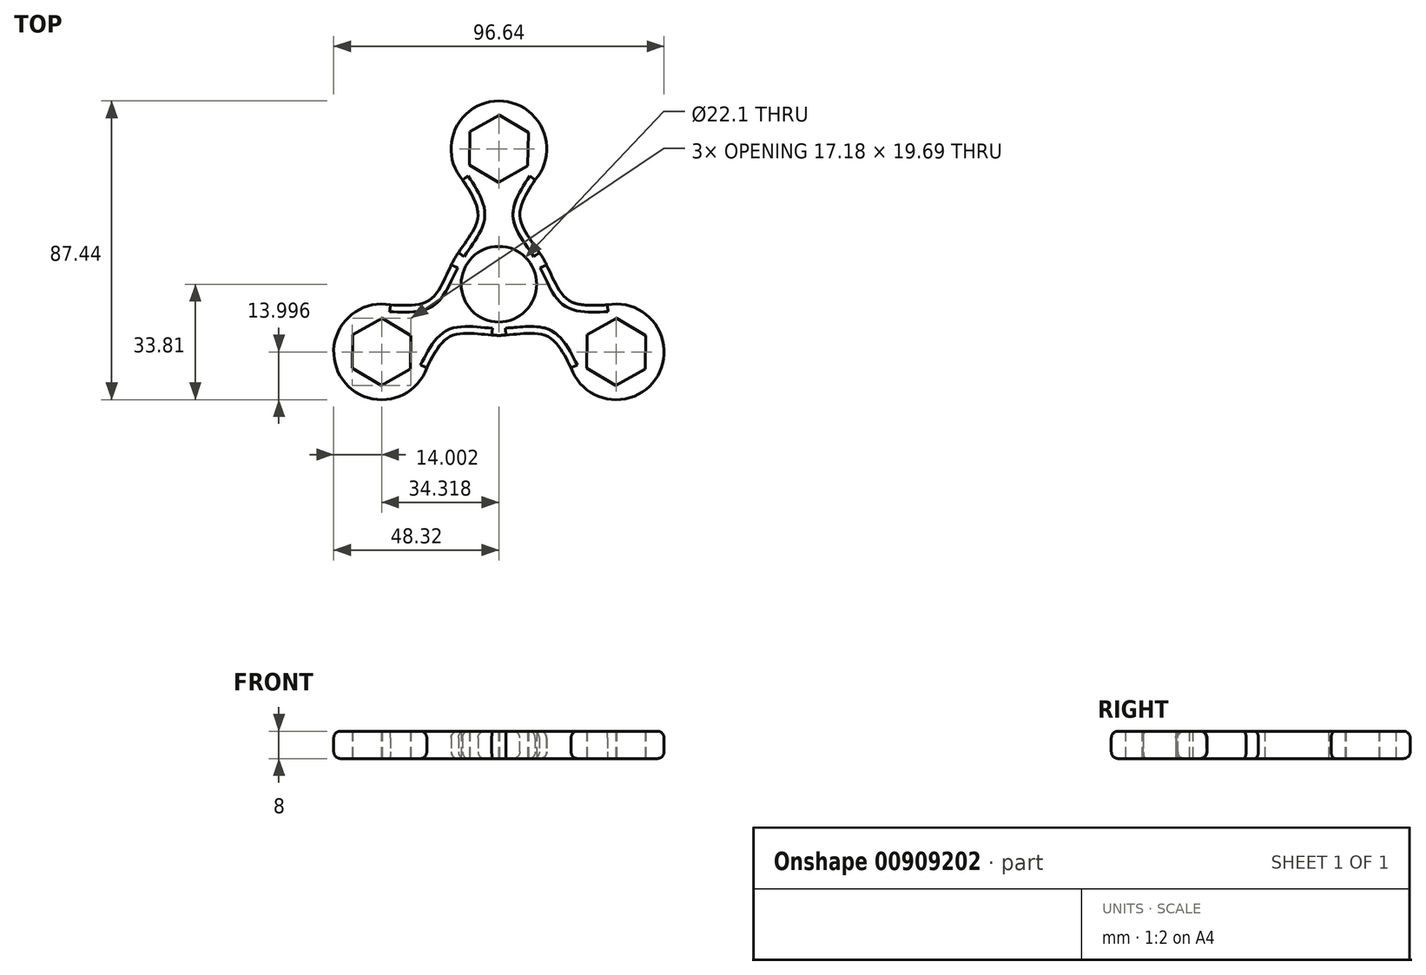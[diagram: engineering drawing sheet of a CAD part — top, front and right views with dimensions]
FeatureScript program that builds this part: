
annotation { "Feature Type Name" : "Feature", "Feature Type Description" : "" }
export const myFeature = defineFeature(function(context is Context, id is Id, definition is map)
    precondition{}
    {
        {
            var Q0;
            Q0=qCreatedBy(makeId("Top.planeOp"),FACE);
            var sketch = newSketch(context, id + "F0", { "sketchPlane" : qUnion([Q0])});
            skCircle(sketch, "E0", {"center": v(0, 0) * mm, "radius": 11.05 * mm});
            skLineSegment(sketch, "E1.left", {"start": v(-11.05, 0) * mm, "end": v(-11.05, 0) * mm});
            skLineSegment(sketch, "E1.right", {"start": v(11.05, 0) * mm, "end": v(11.05, 0) * mm});
            skCircle(sketch, "E2.cCircle", {"center": v(0, 39.63) * mm, "radius": 8.53 * mm, "construction": true});
            skLineSegment(sketch, "E2.0", {"start": v(8.46, 34.59) * mm, "end": v(-0.13, 29.78) * mm});
            skLineSegment(sketch, "E2.1", {"start": v(-0.13, 29.78) * mm, "end": v(-8.6, 34.82) * mm});
            skLineSegment(sketch, "E2.2", {"start": v(-8.6, 34.82) * mm, "end": v(-8.46, 44.67) * mm});
            skLineSegment(sketch, "E2.3", {"start": v(-8.46, 44.67) * mm, "end": v(0.13, 49.47) * mm});
            skLineSegment(sketch, "E2.4", {"start": v(0.13, 49.47) * mm, "end": v(8.6, 44.43) * mm});
            skLineSegment(sketch, "E2.5", {"start": v(8.6, 44.43) * mm, "end": v(8.46, 34.59) * mm});
            skPoint(sketch, "E2.0.midPoint", {"position": v(4.16, 32.19) * mm});
            skCircle(sketch, "E3", {"center": v(0, 39.63) * mm, "radius": 14 * mm});
            skCircle(sketch, "E4", {"center": v(0, 0) * mm, "radius": 15 * mm});
            skFitSpline(sketch, "E5", {"points": [v(-10.6, 30.5) * mm, v(-6.13, 19.92) * mm, v(-11.83, 9.23) * mm], "startDerivative": vector(13.72, -21.36) * mm, "endDerivative": vector(-14.4, -22.42) * mm});
            skFitSpline(sketch, "E6.MirrorCS", {"points": [v(10.6, 30.5) * mm, v(6.13, 19.92) * mm, v(11.83, 9.23) * mm], "startDerivative": vector(-13.72, -21.36) * mm, "endDerivative": vector(14.4, -22.42) * mm});
            skSolve(sketch);
        }
        {
            var Q0;
            Q0=makeQuery(id+"F0.imprint","IMPRINT",FACE,{"disambiguationData":[TD([[makeQuery(id+"F0.imprint","IMPRINT",EDGE,{"derivedFrom":sQuery(id+"F0.wireOp",EDGE,"E2.0")}),1.0]])]});
            var Q1;
            Q1=makeQuery(id+"F0.imprint","IMPRINT",FACE,{"disambiguationData":[TD([[makeQuery(id+"F0.imprint","IMPRINT",EDGE,{"derivedFrom":sQuery(id+"F0.wireOp",EDGE,"E0")}),-1.0]])]});
            var Q2;
            {var subQ0=sQuery(id+"F0.wireOp",EDGE,"E5");Q2=makeQuery(id+"F0.imprint","IMPRINT",FACE,{"disambiguationData":[TD([[makeQuery(id+"F0.imprint","IMPRINT",EDGE,{"derivedFrom":subQ0}),1.0]])]});}
            extrude(context, id + "F1", {"entities" : qUnion([Q0, Q1, Q2]), "depth" : 8 * mm, "offsetDistance" : 25 * mm});
        }
        {
            var Q0;
            Q0=makeQuery(id+"F1.opExtrude","SWEPT_BODY",BODY,{"disambiguationData":[OSD([sQuery(id+"F0.wireOp",EDGE,"E0"),sQuery(id+"F0.wireOp",EDGE,"E2.0"),sQuery(id+"F0.wireOp",EDGE,"E2.1"),sQuery(id+"F0.wireOp",EDGE,"E2.2"),sQuery(id+"F0.wireOp",EDGE,"E2.3"),sQuery(id+"F0.wireOp",EDGE,"E2.4"),sQuery(id+"F0.wireOp",EDGE,"E2.5"),sQuery(id+"F0.wireOp",EDGE,"E3"),sQuery(id+"F0.wireOp",EDGE,"E4"),sQuery(id+"F0.wireOp",EDGE,"E5"),sQuery(id+"F0.wireOp",EDGE,"E6.MirrorCS")])]});
            var Q1;
            Q1=sQuery(id+"F0.wireOp",EDGE,"E0");
            circularPattern(context, id + "F2", {"operationType" : NewBodyOperationType.ADD, "entities" : qUnion([Q0]), "axis" : qUnion([Q1]), "angle" : 360 * degree, "instanceCount" : 3, "equalSpace" : true});
        }
        {
            var Q0;
            Q0=makeQuery(id+"F1.opExtrude","CAP_EDGE",EDGE,{"disambiguationData":[OSD([sQuery(id+"F0.wireOp",EDGE,"E3")])],"isStart":false});
            var Q1;
            Q1=makeQuery(id+"F1.opExtrude","CAP_EDGE",EDGE,{"disambiguationData":[OSD([sQuery(id+"F0.wireOp",EDGE,"E5")])],"isStart":false});
            var Q2;
            Q2=makeQuery(id+"F1.opExtrude","CAP_EDGE",EDGE,{"disambiguationData":[OSD([sQuery(id+"F0.wireOp",EDGE,"E4")])],"isStart":false});
            var Q3;
            Q3=makeQuery(id+"F2.opPattern","COPY",EDGE,{"derivedFrom":makeQuery(id+"F1.opExtrude","CAP_EDGE",EDGE,{"disambiguationData":[OSD([sQuery(id+"F0.wireOp",EDGE,"E6.MirrorCS")])],"isStart":false}),"instanceName":"1"});
            var Q4;
            Q4=makeQuery(id+"F2.opPattern","COPY",EDGE,{"derivedFrom":makeQuery(id+"F1.opExtrude","CAP_EDGE",EDGE,{"disambiguationData":[OSD([sQuery(id+"F0.wireOp",EDGE,"E3")])],"isStart":false}),"instanceName":"1"});
            var Q5;
            Q5=makeQuery(id+"F1.opExtrude","CAP_EDGE",EDGE,{"disambiguationData":[OSD([sQuery(id+"F0.wireOp",EDGE,"E6.MirrorCS")])],"isStart":false});
            var Q6;
            Q6=makeQuery(id+"F2.opPattern","COPY",EDGE,{"derivedFrom":makeQuery(id+"F1.opExtrude","CAP_EDGE",EDGE,{"disambiguationData":[OSD([sQuery(id+"F0.wireOp",EDGE,"E5")])],"isStart":false}),"instanceName":"2"});
            var Q7;
            Q7=makeQuery(id+"F2.opPattern","COPY",EDGE,{"derivedFrom":makeQuery(id+"F1.opExtrude","CAP_EDGE",EDGE,{"disambiguationData":[OSD([sQuery(id+"F0.wireOp",EDGE,"E3")])],"isStart":false}),"instanceName":"2"});
            var Q8;
            Q8=makeQuery(id+"F2.opPattern","COPY",EDGE,{"derivedFrom":makeQuery(id+"F1.opExtrude","CAP_EDGE",EDGE,{"disambiguationData":[OSD([sQuery(id+"F0.wireOp",EDGE,"E6.MirrorCS")])],"isStart":false}),"instanceName":"2"});
            var Q9;
            Q9=makeQuery(id+"F2.opPattern","COPY",EDGE,{"derivedFrom":makeQuery(id+"F1.opExtrude","CAP_EDGE",EDGE,{"disambiguationData":[OSD([sQuery(id+"F0.wireOp",EDGE,"E4")])],"isStart":false}),"instanceName":"1"});
            var Q10;
            Q10=makeQuery(id+"F2.opPattern","COPY",EDGE,{"derivedFrom":makeQuery(id+"F1.opExtrude","CAP_EDGE",EDGE,{"disambiguationData":[OSD([sQuery(id+"F0.wireOp",EDGE,"E5")])],"isStart":false}),"instanceName":"1"});
            fillet(context, id + "F3", {"entities" : qUnion([Q0, Q1, Q2, Q3, Q4, Q5, Q6, Q7, Q8, Q9, Q10]), "radius" : 2 * mm, "tangentPropagation" : true, "allowEdgeOverflow" : false});
        }
        {
            var Q0;
            Q0=makeQuery(id+"F2.opPattern","COPY",EDGE,{"derivedFrom":makeQuery(id+"F1.opExtrude","CAP_EDGE",EDGE,{"disambiguationData":[OSD([sQuery(id+"F0.wireOp",EDGE,"E3")])],"isStart":true}),"instanceName":"2"});
            var Q1;
            Q1=makeQuery(id+"F2.opPattern","COPY",EDGE,{"derivedFrom":makeQuery(id+"F1.opExtrude","CAP_EDGE",EDGE,{"disambiguationData":[OSD([sQuery(id+"F0.wireOp",EDGE,"E5")])],"isStart":true}),"instanceName":"2"});
            var Q2;
            Q2=makeQuery(id+"F2.opPattern","COPY",EDGE,{"derivedFrom":makeQuery(id+"F1.opExtrude","CAP_EDGE",EDGE,{"disambiguationData":[OSD([sQuery(id+"F0.wireOp",EDGE,"E6.MirrorCS")])],"isStart":true}),"instanceName":"2"});
            var Q3;
            Q3=makeQuery(id+"F2.opPattern","COPY",EDGE,{"derivedFrom":makeQuery(id+"F1.opExtrude","CAP_EDGE",EDGE,{"disambiguationData":[OSD([sQuery(id+"F0.wireOp",EDGE,"E5")])],"isStart":true}),"instanceName":"1"});
            var Q4;
            {var subQ0=sQuery(id+"F0.wireOp",EDGE,"E5");var subQ2=sQuery(id+"F0.wireOp",EDGE,"E4");Q4=makeQuery(id+"F2.boolean.opBoolean","SPLIT",EDGE,{"disambiguationData":[TD([makeQuery(id+"F2.opPattern","COPY",FACE,{"derivedFrom":makeQuery(id+"F1.opExtrude","SWEPT_FACE",FACE,{"disambiguationData":[OSD([subQ0])]}),"instanceName":"1"})])],"derivedFrom":makeQuery(id+"F1.opExtrude","CAP_EDGE",EDGE,{"disambiguationData":[OSD([subQ2])],"isStart":true})});}
            var Q5;
            Q5=makeQuery(id+"F2.opPattern","COPY",EDGE,{"derivedFrom":makeQuery(id+"F1.opExtrude","CAP_EDGE",EDGE,{"disambiguationData":[OSD([sQuery(id+"F0.wireOp",EDGE,"E6.MirrorCS")])],"isStart":true}),"instanceName":"1"});
            var Q6;
            Q6=makeQuery(id+"F2.opPattern","COPY",EDGE,{"derivedFrom":makeQuery(id+"F1.opExtrude","CAP_EDGE",EDGE,{"disambiguationData":[OSD([sQuery(id+"F0.wireOp",EDGE,"E3")])],"isStart":true}),"instanceName":"1"});
            var Q7;
            Q7=makeQuery(id+"F1.opExtrude","CAP_EDGE",EDGE,{"disambiguationData":[OSD([sQuery(id+"F0.wireOp",EDGE,"E6.MirrorCS")])],"isStart":true});
            var Q8;
            {var subQ0=sQuery(id+"F0.wireOp",EDGE,"E6.MirrorCS");var subQ2=sQuery(id+"F0.wireOp",EDGE,"E4");Q8=makeQuery(id+"F2.boolean.opBoolean","SPLIT",EDGE,{"disambiguationData":[TD([makeQuery(id+"F1.opExtrude","SWEPT_FACE",FACE,{"disambiguationData":[OSD([subQ0])]})])],"derivedFrom":makeQuery(id+"F1.opExtrude","CAP_EDGE",EDGE,{"disambiguationData":[OSD([subQ2])],"isStart":true})});}
            var Q9;
            {var subQ1=sQuery(id+"F0.wireOp",EDGE,"E5");var subQ2=sQuery(id+"F0.wireOp",EDGE,"E4");Q9=makeQuery(id+"F2.boolean.opBoolean","SPLIT",EDGE,{"disambiguationData":[TD([makeQuery(id+"F1.opExtrude","SWEPT_FACE",FACE,{"disambiguationData":[OSD([subQ1])]})])],"derivedFrom":makeQuery(id+"F1.opExtrude","CAP_EDGE",EDGE,{"disambiguationData":[OSD([subQ2])],"isStart":true})});}
            var Q10;
            Q10=makeQuery(id+"F1.opExtrude","CAP_EDGE",EDGE,{"disambiguationData":[OSD([sQuery(id+"F0.wireOp",EDGE,"E5")])],"isStart":true});
            var Q11;
            Q11=makeQuery(id+"F1.opExtrude","CAP_EDGE",EDGE,{"disambiguationData":[OSD([sQuery(id+"F0.wireOp",EDGE,"E3")])],"isStart":true});
            fillet(context, id + "F4", {"entities" : qUnion([Q0, Q1, Q2, Q3, Q4, Q5, Q6, Q7, Q8, Q9, Q10, Q11]), "radius" : 2 * mm, "tangentPropagation" : true, "allowEdgeOverflow" : false});
        }
    });
